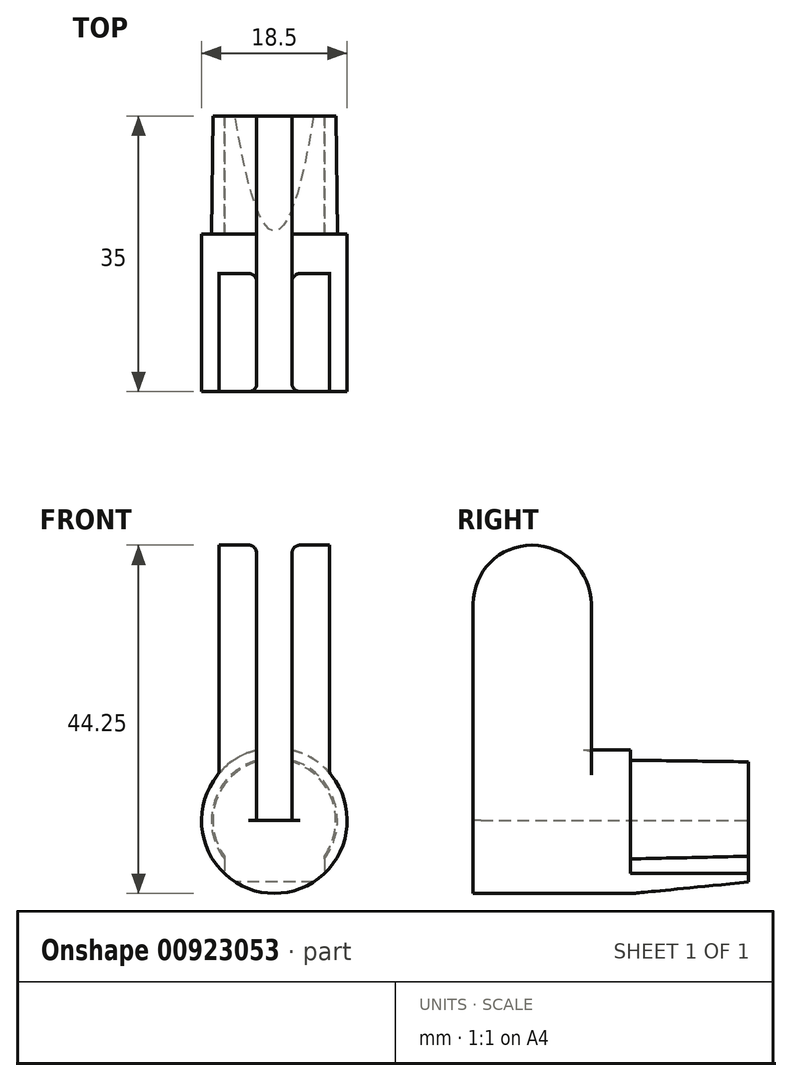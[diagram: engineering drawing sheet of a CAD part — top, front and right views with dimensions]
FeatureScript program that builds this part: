
annotation { "Feature Type Name" : "Feature", "Feature Type Description" : "" }
export const myFeature = defineFeature(function(context is Context, id is Id, definition is map)
    precondition{}
    {
        {
            var Q0;
            Q0=qCreatedBy(makeId("Front.planeOp"),FACE);
            var sketch = newSketch(context, id + "F0", { "sketchPlane" : qUnion([Q0])});
            skCircle(sketch, "E0", {"center": v(0, 0) * mm, "radius": 7.8 * mm});
            skSolve(sketch);
        }
        {
            var Q0;
            Q0 = qSketchRegion(id + "F0", true);
            extrude(context, id + "F1", {"entities" : qUnion([Q0]), "depth" : 15 * mm, "offsetDistance" : 25 * mm});
        }
        {
            var Q0;
            Q0=makeQuery(id+"F1.opExtrude","CAP_FACE",FACE,{"disambiguationData":[OSD([sQuery(id+"F0.wireOp",EDGE,"E0")])],"isStart":false});
            var sketch = newSketch(context, id + "F2", { "sketchPlane" : qUnion([Q0])});
            skCircle(sketch, "E1", {"center": v(0, 0) * mm, "radius": 8 * mm});
            skSolve(sketch);
        }
        {
            var Q1;
            Q1 = qSketchRegion(id + "F0", true);
            var Q2;
            Q2 = qSketchRegion(id + "F2", true);
            loft(context, id + "F3", {"operationType" : NewBodyOperationType.ADD, "sheetProfilesArray" : [{ "sheetProfileEntities" : qUnion([Q1]) }, { "sheetProfileEntities" : qUnion([Q2]) }]});
        }
        {
            var Q0;
            Q0=makeQuery(id+"F1.opExtrude","CAP_FACE",FACE,{"disambiguationData":[OSD([sQuery(id+"F0.wireOp",EDGE,"E0")])],"isStart":false});
            var sketch = newSketch(context, id + "F4", { "sketchPlane" : qUnion([Q0])});
            skCircle(sketch, "E2", {"center": v(0, 0) * mm, "radius": 9.25 * mm});
            skSolve(sketch);
        }
        {
            var Q0;
            Q0 = qSketchRegion(id + "F4", true);
            extrude(context, id + "F5", {"entities" : qUnion([Q0]), "operationType" : NewBodyOperationType.ADD, "depth" : 20 * mm, "offsetDistance" : 25 * mm});
        }
        {
            var Q0;
            Q0=makeQuery(id+"F5.opExtrude","CAP_FACE",FACE,{"disambiguationData":[OSD([sQuery(id+"F4.wireOp",EDGE,"E2")])],"isStart":true});
            var sketch = newSketch(context, id + "F6", { "sketchPlane" : qUnion([Q0])});
            skLineSegment(sketch, "E3", {"start": v(-6.35, -4.53) * mm, "end": v(-6.35, -6.73) * mm});
            skLineSegment(sketch, "E4", {"start": v(6.35, -4.53) * mm, "end": v(6.35, -6.73) * mm});
            skLineSegment(sketch, "E5", {"start": v(-6.35, -4.53) * mm, "end": v(6.35, -4.53) * mm});
            skSolve(sketch);
        }
        {
            var Q0;
            {var subQ0=sQuery(id+"F6.wireOp",EDGE,"E3");Q0=makeQuery(id+"F6.imprint","IMPRINT",FACE,{"disambiguationData":[TD([[makeQuery(id+"F6.imprint","IMPRINT",EDGE,{"derivedFrom":subQ0}),1.0]])]});}
            extrude(context, id + "F7", {"entities" : qUnion([Q0]), "operationType" : NewBodyOperationType.ADD, "depth" : 15 * mm, "offsetDistance" : 25 * mm});
        }
        {
            var Q0;
            Q0=qCreatedBy(makeId("Right.planeOp"),FACE);
            var sketch = newSketch(context, id + "F8", { "sketchPlane" : qUnion([Q0])});
            skLineSegment(sketch, "E6.bottom", {"start": v(-20, 0) * mm, "end": v(-35, 0) * mm});
            skLineSegment(sketch, "E6.top", {"start": v(-20, 16) * mm, "end": v(-35, 16) * mm});
            skLineSegment(sketch, "E6.left", {"start": v(-20, 0) * mm, "end": v(-20, 16) * mm});
            skLineSegment(sketch, "E6.right", {"start": v(-35, 0) * mm, "end": v(-35, 16) * mm});
            skCircle(sketch, "E7", {"center": v(-27.5, 16) * mm, "radius": 7.5 * mm});
            skSolve(sketch);
        }
        {
            var Q0;
            Q0 = qSketchRegion(id + "F8", true);
            extrude(context, id + "F9", {"entities" : qUnion([Q0]), "operationType" : NewBodyOperationType.ADD, "endBound" : BoundingType.SYMMETRIC, "depth" : 14 * mm, "offsetDistance" : 25 * mm});
        }
        {
            var Q0;
            Q0=qCreatedBy(makeId("Right.planeOp"),FACE);
            var sketch = newSketch(context, id + "F10", { "sketchPlane" : qUnion([Q0])});
            skLineSegment(sketch, "E8.bottom", {"start": v(-35, 0) * mm, "end": v(-20, 0) * mm});
            skLineSegment(sketch, "E8.top", {"start": v(-35, 27.5) * mm, "end": v(-20, 27.5) * mm});
            skLineSegment(sketch, "E8.left", {"start": v(-35, 0) * mm, "end": v(-35, 27.5) * mm});
            skLineSegment(sketch, "E8.right", {"start": v(-20, 0) * mm, "end": v(-20, 27.5) * mm});
            skCircle(sketch, "E9", {"center": v(-27.5, 27.5) * mm, "radius": 7.5 * mm});
            skSolve(sketch);
        }
        {
            var Q0;
            Q0 = qSketchRegion(id + "F10", true);
            extrude(context, id + "F11", {"entities" : qUnion([Q0]), "endBound" : BoundingType.SYMMETRIC, "depth" : 14 * mm, "offsetDistance" : 25 * mm});
        }
        {
            var Q0;
            Q0=qCreatedBy(makeId("Front.planeOp"),FACE);
            var sketch = newSketch(context, id + "F12", { "sketchPlane" : qUnion([Q0])});
            skLineSegment(sketch, "E10.bottom", {"start": v(-2.25, 35) * mm, "end": v(2.25, 35) * mm});
            skLineSegment(sketch, "E10.top", {"start": v(-2.25, 0) * mm, "end": v(2.25, 0) * mm});
            skLineSegment(sketch, "E10.left", {"start": v(-2.25, 35) * mm, "end": v(-2.25, 0) * mm});
            skLineSegment(sketch, "E10.right", {"start": v(2.25, 35) * mm, "end": v(2.25, 0) * mm});
            skSolve(sketch);
        }
        {
            var Q0;
            Q0 = qSketchRegion(id + "F12", true);
            extrude(context, id + "F13", {"entities" : qUnion([Q0]), "operationType" : NewBodyOperationType.REMOVE, "depth" : 40 * mm, "offsetDistance" : 25 * mm});
        }
        {
            var Q0;
            Q0=makeQuery(id+"F1.opExtrude","SWEPT_BODY",BODY,{"disambiguationData":[OSD([sQuery(id+"F0.wireOp",EDGE,"E0")])]});
            var Q1;
            Q1=makeQuery(id+"F13.boolean.opBoolean","SPLIT",BODY,{"disambiguationData":[OD(0.0)],"derivedFrom":makeQuery(id+"F11.opExtrude","SWEPT_BODY",BODY,{"disambiguationData":[OSD([sQuery(id+"F10.wireOp",EDGE,"E8.bottom"),sQuery(id+"F10.wireOp",EDGE,"E8.left"),sQuery(id+"F10.wireOp",EDGE,"E8.right"),sQuery(id+"F10.wireOp",EDGE,"E9")])]})});
            var Q2;
            Q2=makeQuery(id+"F13.boolean.opBoolean","SPLIT",BODY,{"disambiguationData":[OD(1.0)],"derivedFrom":makeQuery(id+"F11.opExtrude","SWEPT_BODY",BODY,{"disambiguationData":[OSD([sQuery(id+"F10.wireOp",EDGE,"E8.bottom"),sQuery(id+"F10.wireOp",EDGE,"E8.left"),sQuery(id+"F10.wireOp",EDGE,"E8.right"),sQuery(id+"F10.wireOp",EDGE,"E9")])]})});
            booleanBodies(context, id + "F14", {"operationType" : BooleanOperationType.UNION, "tools" : qUnion([Q0, Q1, Q2])});
        }
        {
            var Q0;
            Q0=makeQuery(id+"F13.boolean.opBoolean","INTERSECT",EDGE,{"derivedFrom":[makeQuery(id+"F11.opExtrude","SWEPT_FACE",FACE,{"disambiguationData":[OSD([sQuery(id+"F10.wireOp",EDGE,"E9")])]}),makeQuery(id+"F13.opExtrude","SWEPT_FACE",FACE,{"disambiguationData":[OSD([sQuery(id+"F12.wireOp",EDGE,"E10.right")])]})]});
            var Q1;
            Q1=makeQuery(id+"F13.boolean.opBoolean","INTERSECT",EDGE,{"derivedFrom":[makeQuery(id+"F11.opExtrude","SWEPT_FACE",FACE,{"disambiguationData":[OSD([sQuery(id+"F10.wireOp",EDGE,"E9")])]}),makeQuery(id+"F13.opExtrude","SWEPT_FACE",FACE,{"disambiguationData":[OSD([sQuery(id+"F12.wireOp",EDGE,"E10.left")])]})]});
            var Q2;
            Q2=makeQuery(id+"F14.opBoolean","INTERSECT",EDGE,{"derivedFrom":[makeQuery(id+"F9.opExtrude","SWEPT_FACE",FACE,{"disambiguationData":[OSD([sQuery(id+"F8.wireOp",EDGE,"E7")])]}),makeQuery(id+"F13.boolean.opBoolean","COPY",FACE,{"derivedFrom":makeQuery(id+"F13.opExtrude","SWEPT_FACE",FACE,{"disambiguationData":[OSD([sQuery(id+"F12.wireOp",EDGE,"E10.left")])]})})]});
            var Q3;
            Q3=makeQuery(id+"F14.opBoolean","INTERSECT",EDGE,{"derivedFrom":[makeQuery(id+"F9.opExtrude","SWEPT_FACE",FACE,{"disambiguationData":[OSD([sQuery(id+"F8.wireOp",EDGE,"E7")])]}),makeQuery(id+"F13.boolean.opBoolean","COPY",FACE,{"derivedFrom":makeQuery(id+"F13.opExtrude","SWEPT_FACE",FACE,{"disambiguationData":[OSD([sQuery(id+"F12.wireOp",EDGE,"E10.right")])]})})]});
            var Q4;
            {var subQ4=sQuery(id+"F10.wireOp",EDGE,"E8.right");var subQ6=makeQuery(id+"F11.opExtrude","SWEPT_FACE",FACE,{"disambiguationData":[OSD([subQ4])]});Q4=makeQuery(id+"F14.opBoolean","INTERSECT",EDGE,{"derivedFrom":[makeQuery(id+"F13.boolean.opBoolean","SPLIT",FACE,{"disambiguationData":[TD([makeQuery(id+"F13.opExtrude","SWEPT_FACE",FACE,{"disambiguationData":[OSD([sQuery(id+"F12.wireOp",EDGE,"E10.left")])]})])],"derivedFrom":subQ6}),makeQuery(id+"F13.boolean.opBoolean","SPLIT",FACE,{"disambiguationData":[TD([makeQuery(id+"F13.opExtrude","SWEPT_FACE",FACE,{"disambiguationData":[OSD([sQuery(id+"F12.wireOp",EDGE,"E10.right")])]})])],"derivedFrom":subQ6})]});}
            var Q5;
            {var subQ0=sQuery(id+"F4.wireOp",EDGE,"E2");Q5=makeQuery(id+"F9.boolean.opBoolean","INTERSECT",EDGE,{"derivedFrom":[makeQuery(id+"F7.boolean.opBoolean","MERGE",FACE,{"derivedFrom":[makeQuery(id+"F5.opExtrude","SWEPT_FACE",FACE,{"disambiguationData":[OSD([subQ0])]}),makeQuery(id+"F7.opExtrude","SWEPT_FACE",FACE,{"disambiguationData":[OSD([subQ0])]})]}),makeQuery(id+"F9.opExtrude","CAP_FACE",FACE,{"disambiguationData":[OSD([sQuery(id+"F8.wireOp",EDGE,"E6.bottom"),sQuery(id+"F8.wireOp",EDGE,"E6.left"),sQuery(id+"F8.wireOp",EDGE,"E6.right"),sQuery(id+"F8.wireOp",EDGE,"E7")])],"isStart":true})]});}
            var Q6;
            {var subQ0=sQuery(id+"F4.wireOp",EDGE,"E2");Q6=makeQuery(id+"F9.boolean.opBoolean","INTERSECT",EDGE,{"derivedFrom":[makeQuery(id+"F7.boolean.opBoolean","MERGE",FACE,{"derivedFrom":[makeQuery(id+"F5.opExtrude","SWEPT_FACE",FACE,{"disambiguationData":[OSD([subQ0])]}),makeQuery(id+"F7.opExtrude","SWEPT_FACE",FACE,{"disambiguationData":[OSD([subQ0])]})]}),makeQuery(id+"F9.opExtrude","CAP_FACE",FACE,{"disambiguationData":[OSD([sQuery(id+"F8.wireOp",EDGE,"E6.bottom"),sQuery(id+"F8.wireOp",EDGE,"E6.left"),sQuery(id+"F8.wireOp",EDGE,"E6.right"),sQuery(id+"F8.wireOp",EDGE,"E7")])],"isStart":false})]});}
            fillet(context, id + "F15", {"entities" : qUnion([Q0, Q1, Q2, Q3, Q4, Q5, Q6]), "radius" : 1 * mm, "tangentPropagation" : true, "allowEdgeOverflow" : false});
        }
        {
            var Q0;
            Q0=qCreatedBy(makeId("Right.planeOp"),FACE);
            var sketch = newSketch(context, id + "F16", { "sketchPlane" : qUnion([Q0])});
            skLineSegment(sketch, "E11", {"start": v(-15.15, -9.3) * mm, "end": v(0, -9.3) * mm});
            skLineSegment(sketch, "E12", {"start": v(0, -9.3) * mm, "end": v(0, -7.8) * mm});
            skLineSegment(sketch, "E13", {"start": v(0, -7.8) * mm, "end": v(-15.15, -9.3) * mm});
            skSolve(sketch);
        }
        {
            var Q0;
            Q0 = qSketchRegion(id + "F16", true);
            extrude(context, id + "F17", {"entities" : qUnion([Q0]), "operationType" : NewBodyOperationType.REMOVE, "endBound" : BoundingType.SYMMETRIC, "depth" : 30 * mm, "offsetDistance" : 25 * mm});
        }
    });
